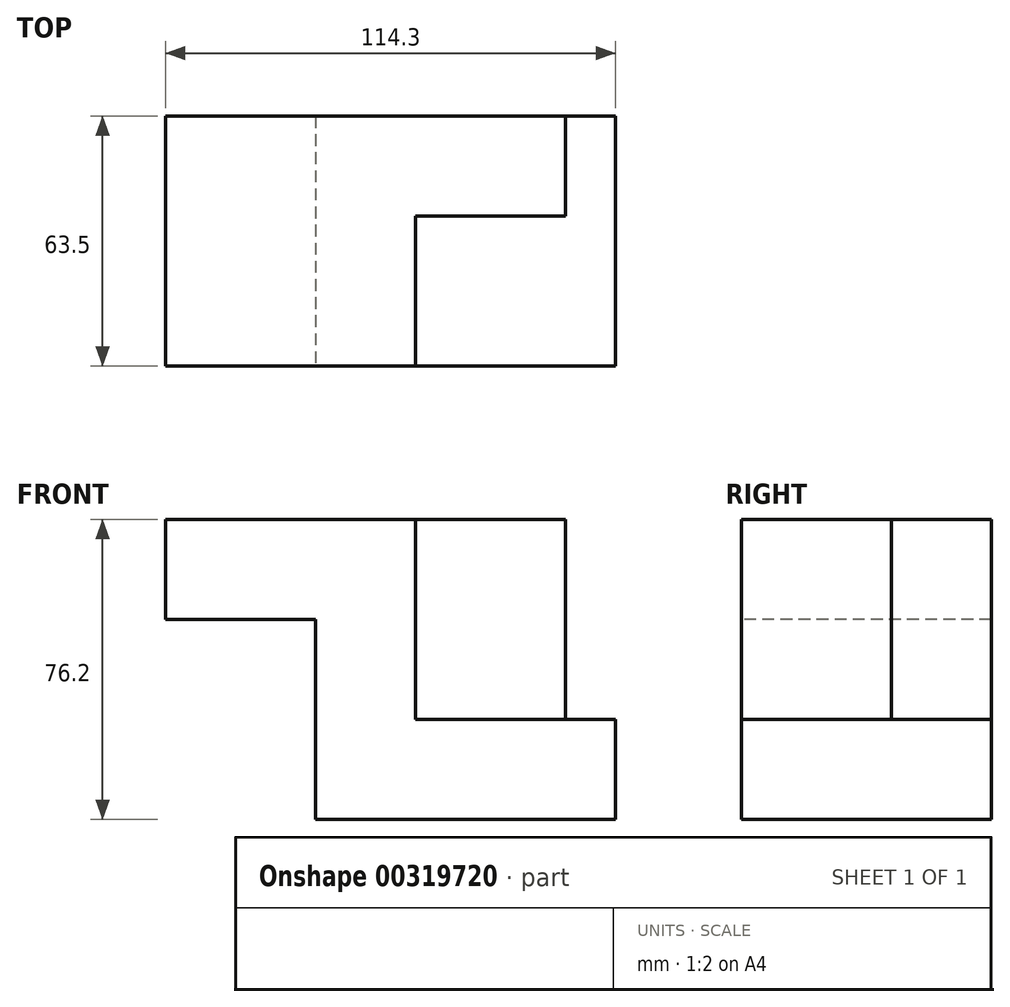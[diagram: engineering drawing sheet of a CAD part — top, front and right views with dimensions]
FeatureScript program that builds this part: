
annotation { "Feature Type Name" : "Feature", "Feature Type Description" : "" }
export const myFeature = defineFeature(function(context is Context, id is Id, definition is map)
    precondition{}
    {
        {
            var Q0;
            Q0=qCreatedBy(makeId("Top.planeOp"),FACE);
            var sketch = newSketch(context, id + "F0", { "sketchPlane" : qUnion([Q0])});
            skLineSegment(sketch, "E0", {"start": v(-31.82, 30.23) * mm, "end": v(-31.82, -33.27) * mm});
            skLineSegment(sketch, "E1", {"start": v(-31.82, -33.27) * mm, "end": v(44.38, -33.27) * mm});
            skLineSegment(sketch, "E2", {"start": v(44.38, -33.27) * mm, "end": v(44.38, 30.23) * mm});
            skLineSegment(sketch, "E3", {"start": v(44.38, 30.23) * mm, "end": v(-31.82, 30.23) * mm});
            skSolve(sketch);
        }
        {
            var Q0;
            Q0=makeQuery(id+"F0.imprint","IMPRINT",FACE,{"disambiguationData":[TD([[makeQuery(id+"F0.imprint","IMPRINT",EDGE,{"derivedFrom":sQuery(id+"F0.wireOp",EDGE,"E0")}),1.0]])]});
            extrude(context, id + "F1", {"entities" : qUnion([Q0]), "depth" : 25.4 * mm});
        }
        {
            var Q0;
            Q0=makeQuery(id+"F1.opExtrude","CAP_FACE",FACE,{"disambiguationData":[OSD([sQuery(id+"F0.wireOp",EDGE,"E0"),sQuery(id+"F0.wireOp",EDGE,"E1"),sQuery(id+"F0.wireOp",EDGE,"E2"),sQuery(id+"F0.wireOp",EDGE,"E3")])],"isStart":false});
            var sketch = newSketch(context, id + "F2", { "sketchPlane" : qUnion([Q0])});
            skLineSegment(sketch, "E4", {"start": v(-31.82, -33.27) * mm, "end": v(-6.42, -33.27) * mm});
            skLineSegment(sketch, "E5", {"start": v(-6.42, -33.27) * mm, "end": v(-6.42, 4.83) * mm});
            skLineSegment(sketch, "E6", {"start": v(-6.42, 4.83) * mm, "end": v(31.68, 4.83) * mm});
            skLineSegment(sketch, "E7", {"start": v(31.68, 4.83) * mm, "end": v(31.68, 30.23) * mm});
            skSolve(sketch);
        }
        {
            var Q0;
            Q0=makeQuery(id+"F2.imprint","IMPRINT",FACE,{"disambiguationData":[TD([[makeQuery(id+"F2.imprint","IMPRINT",EDGE,{"derivedFrom":sQuery(id+"F2.wireOp",EDGE,"E4")}),1.0]])]});
            extrude(context, id + "F3", {"entities" : qUnion([Q0]), "operationType" : NewBodyOperationType.ADD, "depth" : 50.8 * mm});
        }
        {
            var Q0;
            {var subQ0=sQuery(id+"F0.wireOp",EDGE,"E0");Q0=makeQuery(id+"F3.boolean.opBoolean","MERGE",FACE,{"derivedFrom":[makeQuery(id+"F1.opExtrude","SWEPT_FACE",FACE,{"disambiguationData":[OSD([subQ0])]}),makeQuery(id+"F3.opExtrude","SWEPT_FACE",FACE,{"disambiguationData":[OSD([subQ0])]})]});}
            var sketch = newSketch(context, id + "F4", { "sketchPlane" : qUnion([Q0])});
            skLineSegment(sketch, "E8", {"start": v(-30.23, 76.2) * mm, "end": v(-30.23, 50.8) * mm});
            skLineSegment(sketch, "E9", {"start": v(-30.23, 50.8) * mm, "end": v(33.27, 50.8) * mm});
            skLineSegment(sketch, "E10", {"start": v(33.27, 50.8) * mm, "end": v(33.27, 76.2) * mm});
            skLineSegment(sketch, "E11", {"start": v(33.27, 76.2) * mm, "end": v(-30.23, 76.2) * mm});
            skSolve(sketch);
        }
        {
            var Q0;
            Q0=makeQuery(id+"F4.imprint","IMPRINT",FACE,{"disambiguationData":[TD([[makeQuery(id+"F4.imprint","IMPRINT",EDGE,{"derivedFrom":sQuery(id+"F4.wireOp",EDGE,"E8")}),1.0]])]});
            extrude(context, id + "F5", {"entities" : qUnion([Q0]), "operationType" : NewBodyOperationType.ADD, "depth" : 38.1 * mm});
        }
    });
